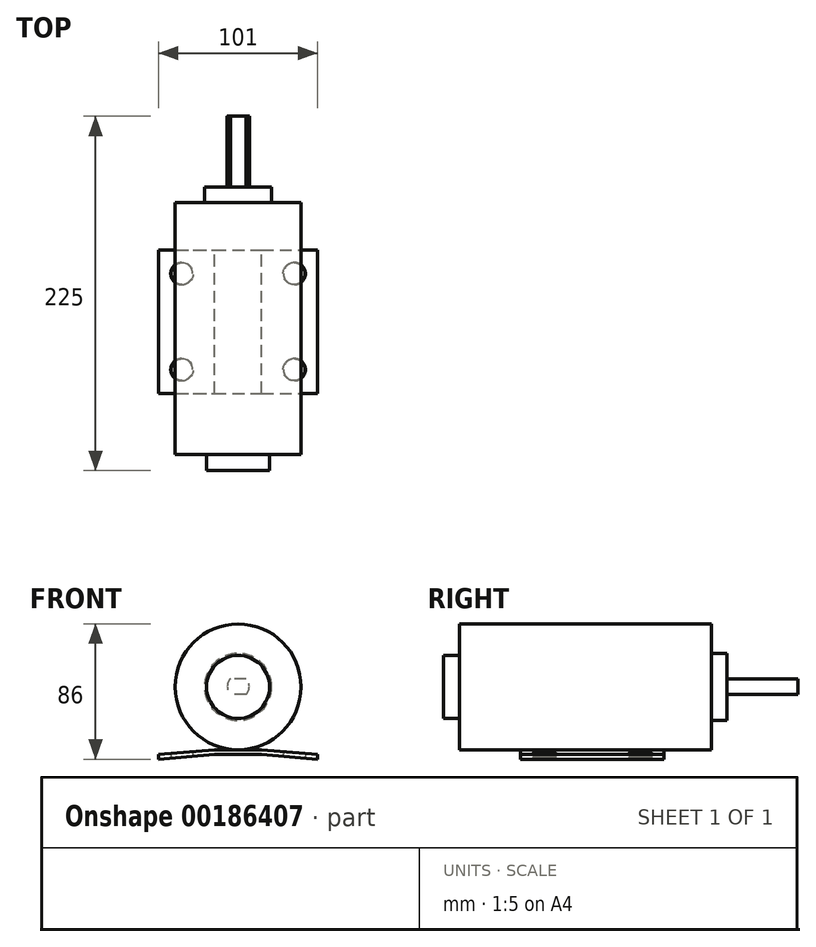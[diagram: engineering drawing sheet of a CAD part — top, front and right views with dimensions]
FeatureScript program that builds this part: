
annotation { "Feature Type Name" : "Feature", "Feature Type Description" : "" }
export const myFeature = defineFeature(function(context is Context, id is Id, definition is map)
    precondition{}
    {
        {
            var Q0;
            Q0=qCreatedBy(makeId("Front.planeOp"),FACE);
            var sketch = newSketch(context, id + "F0", { "sketchPlane" : qUnion([Q0])});
            skLineSegment(sketch, "E0", {"start": v(-50.5, 0) * mm, "end": v(-50.5, 3) * mm});
            skLineSegment(sketch, "E1", {"start": v(-50.5, 3) * mm, "end": v(-15, 6) * mm});
            skLineSegment(sketch, "E2", {"start": v(15, 6) * mm, "end": v(50.5, 3) * mm});
            skLineSegment(sketch, "E3", {"start": v(50.5, 3) * mm, "end": v(50.5, 0) * mm});
            skLineSegment(sketch, "E4", {"start": v(-50.5, 0) * mm, "end": v(-15, 3) * mm});
            skLineSegment(sketch, "E5", {"start": v(15, 3) * mm, "end": v(50.5, 0) * mm});
            skLineSegment(sketch, "E6", {"start": v(-15, 6) * mm, "end": v(15, 6) * mm});
            skLineSegment(sketch, "E7", {"start": v(-15, 3) * mm, "end": v(15, 3) * mm});
            skSolve(sketch);
        }
        {
            var Q0;
            Q0 = qSketchRegion(id + "F0", true);
            extrude(context, id + "F1", {"entities" : qUnion([Q0]), "depth" : 91 * mm});
        }
        {
            var Q0;
            Q0=makeQuery(id+"F1.opExtrude","SWEPT_FACE",FACE,{"disambiguationData":[OSD([sQuery(id+"F0.wireOp",EDGE,"E4")])]});
            var sketch = newSketch(context, id + "F2", { "sketchPlane" : qUnion([Q0])});
            skPoint(sketch, "E8", {"position": v(-35.32, 76) * mm});
            skPoint(sketch, "E9", {"position": v(-35.32, 15) * mm});
            skSolve(sketch);
        }
        {
            var Q0;
            Q0=makeQuery(id+"F1.opExtrude","SWEPT_FACE",FACE,{"disambiguationData":[OSD([sQuery(id+"F0.wireOp",EDGE,"E5")])]});
            var sketch = newSketch(context, id + "F3", { "sketchPlane" : qUnion([Q0])});
            skPoint(sketch, "E10", {"position": v(35.32, 76) * mm});
            skPoint(sketch, "E11", {"position": v(35.32, 15) * mm});
            skSolve(sketch);
        }
        {
            var Q0;
            Q0=sQuery(id+"F2.wireOp",VERTEX,"E8");
            var Q1;
            Q1=sQuery(id+"F2.wireOp",VERTEX,"E9");
            var Q2;
            Q2=sQuery(id+"F3.wireOp",VERTEX,"E10");
            var Q3;
            Q3=sQuery(id+"F3.wireOp",VERTEX,"E11");
            var Q4;
            Q4=makeQuery(id+"F1.opExtrude","SWEPT_BODY",BODY,{"disambiguationData":[OSD([sQuery(id+"F0.wireOp",EDGE,"E0"),sQuery(id+"F0.wireOp",EDGE,"E1"),sQuery(id+"F0.wireOp",EDGE,"E2"),sQuery(id+"F0.wireOp",EDGE,"E3"),sQuery(id+"F0.wireOp",EDGE,"E4"),sQuery(id+"F0.wireOp",EDGE,"E5"),sQuery(id+"F0.wireOp",EDGE,"E6"),sQuery(id+"F0.wireOp",EDGE,"E7")])]});
            hole(context, id + "F4", {"style" : HoleStyle.SIMPLE, "endStyle" : HoleEndStyle.THROUGH, "holeDiameter" : 14 * mm, "locations" : qUnion([Q0, Q1, Q2, Q3]), "scope" : qUnion([Q4]), "isTappedThrough" : true});
        }
        {
            var Q0;
            Q0=qCreatedBy(makeId("Front.planeOp"),FACE);
            cPlane(context, id + "F5", {"entities" : qUnion([Q0]), "cplaneType" : CPlaneType.OFFSET, "offset" : 30 * mm, "oppositeDirection" : true, "width" : 150 * mm, "height" : 150 * mm});
        }
        {
            var Q0;
            Q0=qCreatedBy(id+"F5.planeOp",FACE);
            var sketch = newSketch(context, id + "F6", { "sketchPlane" : qUnion([Q0])});
            skCircle(sketch, "E12", {"center": v(0, 46) * mm, "radius": 40 * mm});
            skSolve(sketch);
        }
        {
            var Q0;
            Q0=makeQuery(id+"F6.imprint","IMPRINT",FACE,{"disambiguationData":[TD([[makeQuery(id+"F6.imprint","IMPRINT",EDGE,{"derivedFrom":sQuery(id+"F6.wireOp",EDGE,"E12")}),1.0]])]});
            var Q1;
            Q1=sQuery(id+"F6.wireOp",EDGE,"E12");
            extrude(context, id + "F7", {"entities" : qUnion([Q0]), "surfaceEntities" : qUnion([Q1]), "depth" : 160 * mm});
        }
        {
            var Q0;
            Q0=makeQuery(id+"F7.opExtrude","CAP_FACE",FACE,{"disambiguationData":[OSD([sQuery(id+"F6.wireOp",EDGE,"E12")])],"isStart":false});
            var sketch = newSketch(context, id + "F8", { "sketchPlane" : qUnion([Q0])});
            skCircle(sketch, "E13", {"center": v(0, 46) * mm, "radius": 20 * mm});
            skSolve(sketch);
        }
        {
            var Q0;
            Q0=makeQuery(id+"F8.imprint","IMPRINT",FACE,{"disambiguationData":[TD([[makeQuery(id+"F8.imprint","IMPRINT",EDGE,{"derivedFrom":sQuery(id+"F8.wireOp",EDGE,"E13")}),1.0]])]});
            extrude(context, id + "F9", {"entities" : qUnion([Q0]), "operationType" : NewBodyOperationType.ADD, "depth" : 10 * mm});
        }
        {
            var Q0;
            Q0=makeQuery(id+"F7.opExtrude","CAP_FACE",FACE,{"disambiguationData":[OSD([sQuery(id+"F6.wireOp",EDGE,"E12")])],"isStart":true});
            var sketch = newSketch(context, id + "F10", { "sketchPlane" : qUnion([Q0])});
            skCircle(sketch, "E14", {"center": v(0, 46) * mm, "radius": 21.25 * mm});
            skSolve(sketch);
        }
        {
            var Q0;
            Q0=makeQuery(id+"F10.imprint","IMPRINT",FACE,{"disambiguationData":[TD([[makeQuery(id+"F10.imprint","IMPRINT",EDGE,{"derivedFrom":sQuery(id+"F10.wireOp",EDGE,"E14")}),1.0]])]});
            extrude(context, id + "F11", {"entities" : qUnion([Q0]), "operationType" : NewBodyOperationType.ADD, "depth" : 10 * mm});
        }
        {
            var Q0;
            Q0=makeQuery(id+"F11.opExtrude","CAP_FACE",FACE,{"disambiguationData":[OSD([sQuery(id+"F10.wireOp",EDGE,"E14")])],"isStart":false});
            var sketch = newSketch(context, id + "F12", { "sketchPlane" : qUnion([Q0])});
            skArc(sketch, "E15", {"start": v(-5.14, 51.16) * mm, "mid": v(-7.14, 46.26) * mm, "end": v(-5.14, 41.36) * mm});
            skLineSegment(sketch, "E16", {"start": v(-5.14, 51.16) * mm, "end": v(4.86, 51.16) * mm});
            skLineSegment(sketch, "E17", {"start": v(-5.14, 41.36) * mm, "end": v(4.86, 41.36) * mm});
            skArc(sketch, "E18.trimOffspring", {"start": v(4.86, 41.36) * mm, "mid": v(6.86, 46.26) * mm, "end": v(4.86, 51.16) * mm});
            skSolve(sketch);
        }
        {
            var Q0;
            Q0 = qSketchRegion(id + "F12", true);
            extrude(context, id + "F13", {"entities" : qUnion([Q0]), "operationType" : NewBodyOperationType.ADD, "depth" : 45 * mm});
        }
    });
